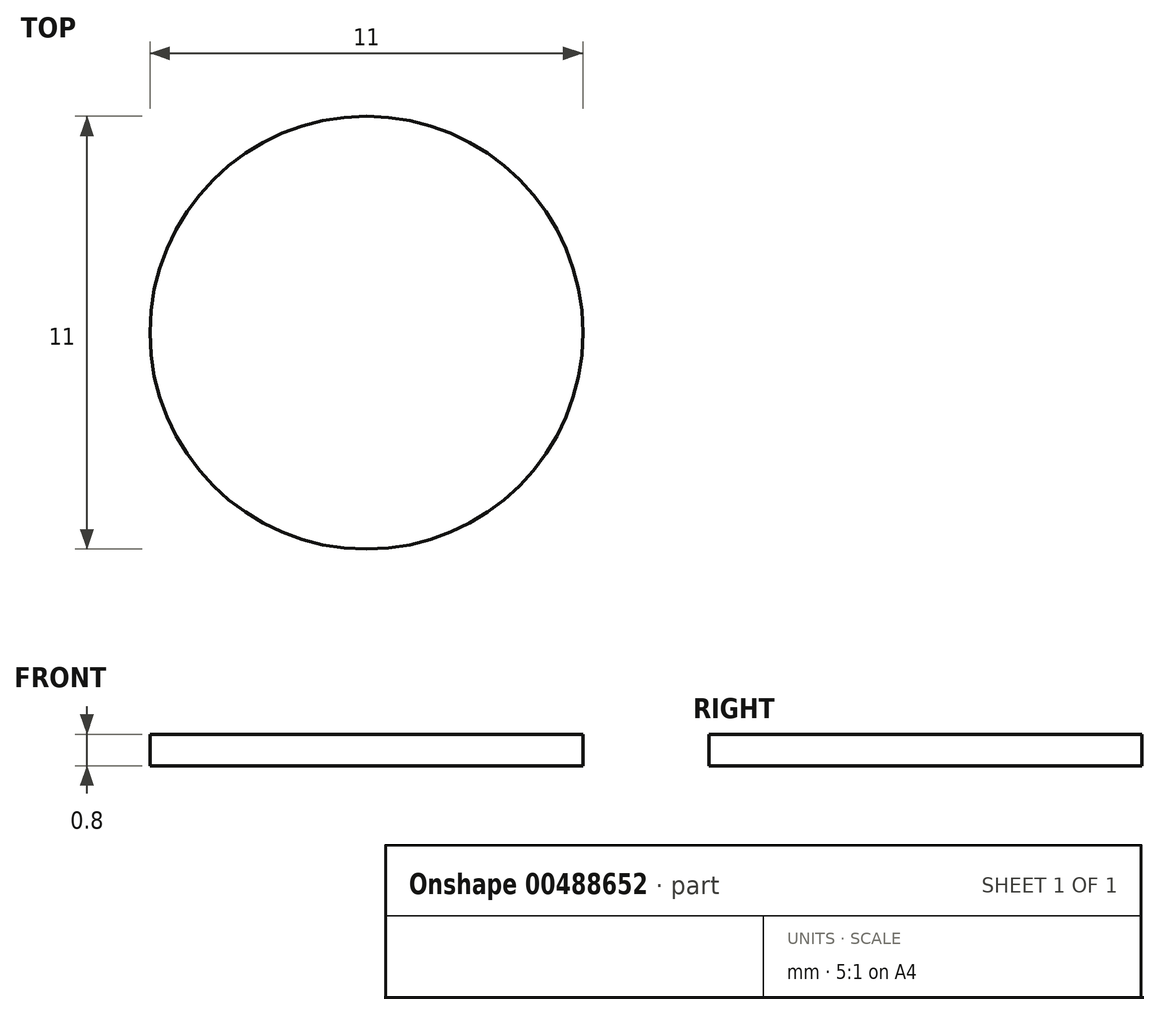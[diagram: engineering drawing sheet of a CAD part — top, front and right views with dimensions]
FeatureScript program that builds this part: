
annotation { "Feature Type Name" : "Feature", "Feature Type Description" : "" }
export const myFeature = defineFeature(function(context is Context, id is Id, definition is map)
    precondition{}
    {
        {
            var Q0;
            Q0=qCreatedBy(makeId("Top.planeOp"),FACE);
            var sketch = newSketch(context, id + "F0", { "sketchPlane" : qUnion([Q0])});
            skCircle(sketch, "E0", {"center": v(0, 0) * mm, "radius": 5.5 * mm});
            skSolve(sketch);
        }
        {
            var Q0;
            Q0=makeQuery(id+"F0.imprint","IMPRINT",FACE,{"disambiguationData":[TD([[makeQuery(id+"F0.imprint","IMPRINT",EDGE,{"derivedFrom":sQuery(id+"F0.wireOp",EDGE,"E0")}),1.0]])]});
            extrude(context, id + "F1", {"entities" : qUnion([Q0]), "depth" : 0.8 * mm});
        }
    });
